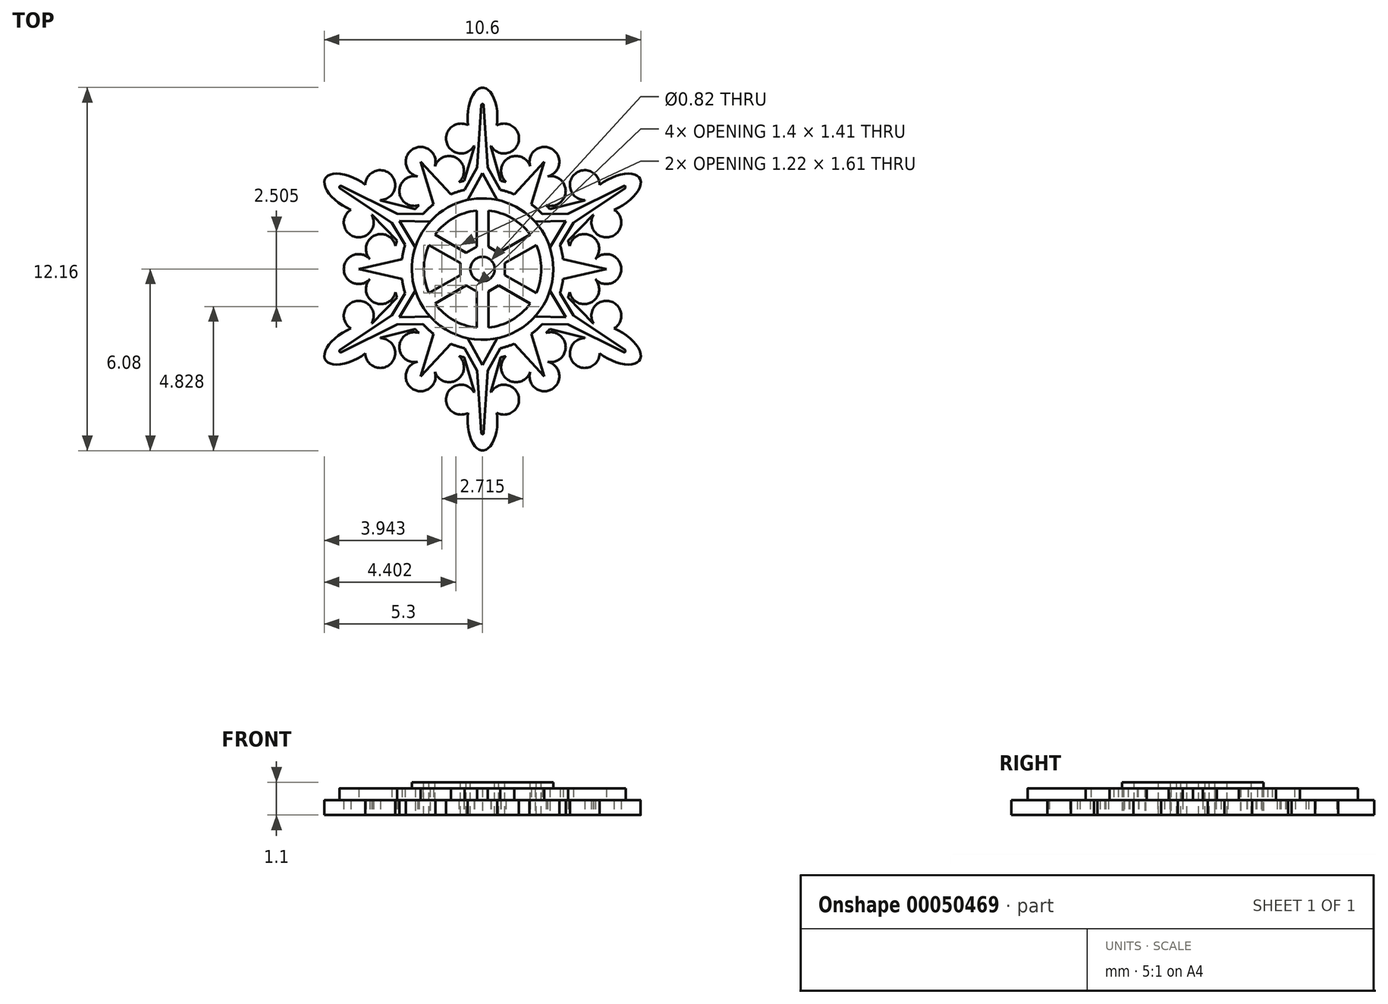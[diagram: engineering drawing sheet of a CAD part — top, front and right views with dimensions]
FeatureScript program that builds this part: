
annotation { "Feature Type Name" : "Feature", "Feature Type Description" : "" }
export const myFeature = defineFeature(function(context is Context, id is Id, definition is map)
    precondition{}
    {
        {
            var Q0;
            Q0=qCreatedBy(makeId("Top.planeOp"),FACE);
            var sketch = newSketch(context, id + "F0", { "sketchPlane" : qUnion([Q0])});
            skArc(sketch, "E0", {"start": v(2.18, 3.1) * mm, "mid": v(2.32, 4.02) * mm, "end": v(1.6, 3.44) * mm});
            skArc(sketch, "E1", {"start": v(2.13, 2.14) * mm, "mid": v(2.78, 2.59) * mm, "end": v(2.18, 3.1) * mm});
            skArc(sketch, "E2", {"start": v(-0.48, 4.81) * mm, "mid": v(-1.2, 4.24) * mm, "end": v(-0.29, 4.12) * mm});
            skLineSegment(sketch, "E3", {"start": v(0, 0) * mm, "end": v(0, 5.06) * mm, "construction": true});
            skLineSegment(sketch, "E4", {"start": v(0, 0) * mm, "end": v(4.69, 2.7) * mm, "construction": true});
            skLineSegment(sketch, "E5", {"start": v(4.69, 2.7) * mm, "end": v(4.69, 0) * mm, "construction": true});
            skLineSegment(sketch, "E6", {"start": v(4.69, 0) * mm, "end": v(0, 0) * mm, "construction": true});
            skArc(sketch, "E7", {"start": v(-0.61, 2.96) * mm, "mid": v(-0.7, 2.94) * mm, "end": v(-0.79, 2.91) * mm});
            skLineSegment(sketch, "E8", {"start": v(0, 0) * mm, "end": v(2.07, 3.6) * mm, "construction": true});
            skLineSegment(sketch, "E9", {"start": v(1.5, 2.61) * mm, "end": v(1.12, 3.29) * mm, "construction": true});
            skLineSegment(sketch, "E10", {"start": v(2.28, 2.61) * mm, "end": v(1.5, 2.61) * mm, "construction": true});
            skLineSegment(sketch, "E11", {"start": v(0, 3.96) * mm, "end": v(-0.72, 4.37) * mm, "construction": true});
            skLineSegment(sketch, "E12", {"start": v(0.72, 4.37) * mm, "end": v(0, 3.96) * mm, "construction": true});
            skArc(sketch, "E13.trimOffspring", {"start": v(0.29, 4.12) * mm, "mid": v(1.2, 4.24) * mm, "end": v(0.48, 4.81) * mm});
            skLineSegment(sketch, "E14.trimOffspring", {"start": v(0.27, 4.11) * mm, "end": v(0.61, 2.96) * mm});
            skLineSegment(sketch, "E15.trimOffspring", {"start": v(-0.27, 4.11) * mm, "end": v(-0.61, 2.96) * mm});
            skLineSegment(sketch, "E16", {"start": v(-0.29, 4.12) * mm, "end": v(-0.27, 4.11) * mm});
            skLineSegment(sketch, "E17", {"start": v(0.29, 4.12) * mm, "end": v(0.27, 4.11) * mm});
            skArc(sketch, "E18.trimOffspring", {"start": v(0.79, 2.91) * mm, "mid": v(0.7, 2.94) * mm, "end": v(0.61, 2.96) * mm});
            skArc(sketch, "E19.trimOffspring", {"start": v(1.6, 3.44) * mm, "mid": v(0.85, 3.7) * mm, "end": v(0.79, 2.91) * mm});
            skEllipticalArc(sketch, "E20", {});
            skArc(sketch, "E21.1.0", {"start": v(-1.6, 3.44) * mm, "mid": v(-2.32, 4.02) * mm, "end": v(-2.18, 3.1) * mm});
            skLineSegment(sketch, "E21.1.1", {"start": v(-3.7, 1.82) * mm, "end": v(-2.86, 0.95) * mm});
            skArc(sketch, "E21.1.2", {"start": v(-2.18, 3.1) * mm, "mid": v(-2.78, 2.59) * mm, "end": v(-2.13, 2.14) * mm});
            skLineSegment(sketch, "E21.1.3", {"start": v(-1.12, 3.29) * mm, "end": v(-1.5, 2.61) * mm, "construction": true});
            skEllipticalArc(sketch, "E21.1.4", {});
            skArc(sketch, "E21.1.5", {"start": v(-0.79, 2.91) * mm, "mid": v(-0.85, 3.7) * mm, "end": v(-1.6, 3.44) * mm});
            skArc(sketch, "E21.1.6", {"start": v(-3.43, 2.31) * mm, "mid": v(-3.07, 3.16) * mm, "end": v(-3.93, 2.82) * mm});
            skArc(sketch, "E21.1.7", {"start": v(-4.4, 1.99) * mm, "mid": v(-4.27, 1.08) * mm, "end": v(-3.71, 1.81) * mm});
            skLineSegment(sketch, "E21.1.8", {"start": v(-3.43, 2.3) * mm, "end": v(-2.25, 2) * mm});
            skLineSegment(sketch, "E21.1.10", {"start": v(-3.7, 1.82) * mm, "end": v(-3.71, 1.81) * mm});
            skLineSegment(sketch, "E21.1.11", {"start": v(-1.5, 2.61) * mm, "end": v(-2.28, 2.61) * mm, "construction": true});
            skLineSegment(sketch, "E21.1.13", {"start": v(-3.43, 2.31) * mm, "end": v(-3.43, 2.3) * mm});
            skArc(sketch, "E21.1.14", {"start": v(-2.13, 2.14) * mm, "mid": v(-2.2, 2.07) * mm, "end": v(-2.25, 2) * mm});
            skArc(sketch, "E21.2.0", {"start": v(-3.78, 0.34) * mm, "mid": v(-4.65, 0) * mm, "end": v(-3.78, -0.34) * mm});
            skLineSegment(sketch, "E21.2.1", {"start": v(-3.43, -2.3) * mm, "end": v(-2.25, -2) * mm});
            skArc(sketch, "E21.2.2", {"start": v(-3.78, -0.34) * mm, "mid": v(-3.63, -1.12) * mm, "end": v(-2.92, -0.77) * mm});
            skLineSegment(sketch, "E21.2.3", {"start": v(-3.4, 0.67) * mm, "end": v(-3.02, 0) * mm, "construction": true});
            skEllipticalArc(sketch, "E21.2.4", {});
            skArc(sketch, "E21.2.5", {"start": v(-2.92, 0.77) * mm, "mid": v(-3.63, 1.12) * mm, "end": v(-3.78, 0.34) * mm});
            skArc(sketch, "E21.2.6", {"start": v(-3.71, -1.81) * mm, "mid": v(-4.27, -1.08) * mm, "end": v(-4.4, -1.99) * mm});
            skArc(sketch, "E21.2.7", {"start": v(-3.93, -2.82) * mm, "mid": v(-3.07, -3.16) * mm, "end": v(-3.43, -2.31) * mm});
            skLineSegment(sketch, "E21.2.8", {"start": v(-3.7, -1.82) * mm, "end": v(-2.86, -0.95) * mm});
            skLineSegment(sketch, "E21.2.10", {"start": v(-3.43, -2.3) * mm, "end": v(-3.43, -2.31) * mm});
            skLineSegment(sketch, "E21.2.11", {"start": v(-3.02, 0) * mm, "end": v(-3.4, -0.67) * mm, "construction": true});
            skLineSegment(sketch, "E21.2.13", {"start": v(-3.71, -1.81) * mm, "end": v(-3.7, -1.82) * mm});
            skArc(sketch, "E21.2.14", {"start": v(-2.92, -0.77) * mm, "mid": v(-2.9, -0.86) * mm, "end": v(-2.86, -0.95) * mm});
            skArc(sketch, "E21.3.0", {"start": v(-2.18, -3.1) * mm, "mid": v(-2.32, -4.02) * mm, "end": v(-1.6, -3.44) * mm});
            skLineSegment(sketch, "E21.3.1", {"start": v(0.27, -4.11) * mm, "end": v(0.61, -2.96) * mm});
            skArc(sketch, "E21.3.2", {"start": v(-1.6, -3.44) * mm, "mid": v(-0.85, -3.7) * mm, "end": v(-0.79, -2.91) * mm});
            skLineSegment(sketch, "E21.3.3", {"start": v(-2.28, -2.61) * mm, "end": v(-1.5, -2.61) * mm, "construction": true});
            skEllipticalArc(sketch, "E21.3.4", {});
            skArc(sketch, "E21.3.5", {"start": v(-2.13, -2.14) * mm, "mid": v(-2.78, -2.59) * mm, "end": v(-2.18, -3.1) * mm});
            skArc(sketch, "E21.3.6", {"start": v(-0.29, -4.12) * mm, "mid": v(-1.2, -4.24) * mm, "end": v(-0.48, -4.81) * mm});
            skArc(sketch, "E21.3.7", {"start": v(0.48, -4.81) * mm, "mid": v(1.2, -4.24) * mm, "end": v(0.29, -4.12) * mm});
            skLineSegment(sketch, "E21.3.8", {"start": v(-0.27, -4.11) * mm, "end": v(-0.61, -2.96) * mm});
            skLineSegment(sketch, "E21.3.10", {"start": v(0.27, -4.11) * mm, "end": v(0.29, -4.12) * mm});
            skLineSegment(sketch, "E21.3.11", {"start": v(-1.5, -2.61) * mm, "end": v(-1.12, -3.29) * mm, "construction": true});
            skLineSegment(sketch, "E21.3.13", {"start": v(-0.29, -4.12) * mm, "end": v(-0.27, -4.11) * mm});
            skArc(sketch, "E21.3.14", {"start": v(-0.79, -2.91) * mm, "mid": v(-0.7, -2.94) * mm, "end": v(-0.61, -2.96) * mm});
            skArc(sketch, "E21.4.0", {"start": v(1.6, -3.44) * mm, "mid": v(2.32, -4.02) * mm, "end": v(2.18, -3.1) * mm});
            skLineSegment(sketch, "E21.4.1", {"start": v(3.7, -1.82) * mm, "end": v(2.86, -0.95) * mm});
            skArc(sketch, "E21.4.2", {"start": v(2.18, -3.1) * mm, "mid": v(2.78, -2.59) * mm, "end": v(2.13, -2.14) * mm});
            skLineSegment(sketch, "E21.4.3", {"start": v(1.12, -3.29) * mm, "end": v(1.5, -2.61) * mm, "construction": true});
            skEllipticalArc(sketch, "E21.4.4", {});
            skArc(sketch, "E21.4.5", {"start": v(0.79, -2.91) * mm, "mid": v(0.85, -3.7) * mm, "end": v(1.6, -3.44) * mm});
            skArc(sketch, "E21.4.6", {"start": v(3.43, -2.31) * mm, "mid": v(3.07, -3.16) * mm, "end": v(3.93, -2.82) * mm});
            skArc(sketch, "E21.4.7", {"start": v(4.4, -1.99) * mm, "mid": v(4.27, -1.08) * mm, "end": v(3.71, -1.81) * mm});
            skLineSegment(sketch, "E21.4.8", {"start": v(3.43, -2.3) * mm, "end": v(2.25, -2) * mm});
            skLineSegment(sketch, "E21.4.10", {"start": v(3.7, -1.82) * mm, "end": v(3.71, -1.81) * mm});
            skLineSegment(sketch, "E21.4.11", {"start": v(1.5, -2.61) * mm, "end": v(2.28, -2.61) * mm, "construction": true});
            skLineSegment(sketch, "E21.4.13", {"start": v(3.43, -2.31) * mm, "end": v(3.43, -2.3) * mm});
            skArc(sketch, "E21.4.14", {"start": v(2.13, -2.14) * mm, "mid": v(2.2, -2.07) * mm, "end": v(2.25, -2) * mm});
            skArc(sketch, "E21.5.0", {"start": v(3.78, -0.34) * mm, "mid": v(4.65, 0) * mm, "end": v(3.78, 0.34) * mm});
            skLineSegment(sketch, "E21.5.1", {"start": v(3.43, 2.3) * mm, "end": v(2.25, 2) * mm});
            skArc(sketch, "E21.5.2", {"start": v(3.78, 0.34) * mm, "mid": v(3.63, 1.12) * mm, "end": v(2.92, 0.77) * mm});
            skLineSegment(sketch, "E21.5.3", {"start": v(3.4, -0.67) * mm, "end": v(3.02, 0) * mm, "construction": true});
            skEllipticalArc(sketch, "E21.5.4", {});
            skArc(sketch, "E21.5.5", {"start": v(2.92, -0.77) * mm, "mid": v(3.63, -1.12) * mm, "end": v(3.78, -0.34) * mm});
            skArc(sketch, "E21.5.6", {"start": v(3.71, 1.81) * mm, "mid": v(4.27, 1.08) * mm, "end": v(4.4, 1.99) * mm});
            skArc(sketch, "E21.5.7", {"start": v(3.93, 2.82) * mm, "mid": v(3.07, 3.16) * mm, "end": v(3.43, 2.31) * mm});
            skLineSegment(sketch, "E21.5.8", {"start": v(3.7, 1.82) * mm, "end": v(2.86, 0.95) * mm});
            skLineSegment(sketch, "E21.5.10", {"start": v(3.43, 2.3) * mm, "end": v(3.43, 2.31) * mm});
            skLineSegment(sketch, "E21.5.11", {"start": v(3.02, 0) * mm, "end": v(3.4, 0.67) * mm, "construction": true});
            skLineSegment(sketch, "E21.5.13", {"start": v(3.71, 1.81) * mm, "end": v(3.7, 1.82) * mm});
            skArc(sketch, "E21.5.14", {"start": v(2.92, 0.77) * mm, "mid": v(2.9, 0.86) * mm, "end": v(2.86, 0.95) * mm});
            skArc(sketch, "E22.trimOffspring", {"start": v(2.25, 2) * mm, "mid": v(2.2, 2.07) * mm, "end": v(2.13, 2.14) * mm});
            skArc(sketch, "E23.trimOffspring", {"start": v(-2.86, 0.95) * mm, "mid": v(-2.9, 0.86) * mm, "end": v(-2.92, 0.77) * mm});
            skArc(sketch, "E24.trimOffspring", {"start": v(2.86, -0.95) * mm, "mid": v(2.9, -0.86) * mm, "end": v(2.92, -0.77) * mm});
            skArc(sketch, "E25.trimOffspring", {"start": v(0.61, -2.96) * mm, "mid": v(0.7, -2.94) * mm, "end": v(0.79, -2.91) * mm});
            skArc(sketch, "E26.trimOffspring", {"start": v(-2.25, -2) * mm, "mid": v(-2.2, -2.07) * mm, "end": v(-2.13, -2.14) * mm});
            skLineSegment(sketch, "E27", {"start": v(3.43, 2.31) * mm, "end": v(3.43, 2.3) * mm});
            const initialGuessF0  = {"E20": [0, 0.005064967554062605, 0, 1, 0.0010143392719328403, 0.0004990733945554542, 4.460182653638514, 1.8230026535410722], "E21.1.4": [-0.0043863905711621475, 0.002532483777031303, -0.8660254037844386, 0.5, 0.0010143392719328403, 0.0004990733945554542, 4.460182653638514, 1.8230026535410722], "E21.2.4": [-0.004386390571162148, -0.002532483777031301, -0.8660254037844388, -0.5, 0.0010143392719328403, 0.0004990733945554542, 4.460182653638514, 1.823002653541072], "E21.3.4": [0, -0.005064967554062605, 0, -1, 0.0010143392719328403, 0.0004990733945554542, 4.460182653638514, 1.8230026535410724], "E21.4.4": [0.004386390571162147, -0.0025324837770313046, 0.8660254037844384, -0.5, 0.0010143392719328403, 0.0004990733945554542, 4.460182653638514, 1.8230026535410724], "E21.5.4": [0.0043863905711621475, 0.002532483777031303, 0.8660254037844386, 0.5, 0.0010143392719328403, 0.0004990733945554542, 4.460182653638514, 1.8230026535410717]};
            skSetInitialGuess(sketch, initialGuessF0);
            skSolve(sketch);
        }
        {
            var Q0;
            Q0 = qSketchRegion(id + "F0", true);
            extrude(context, id + "F1", {"entities" : qUnion([Q0]), "depth" : .5 * mm});
        }
        {
            var Q0;
            Q0=makeQuery(id+"F1.opExtrude","CAP_FACE",FACE,{"disambiguationData":[OSD([sQuery(id+"F0.wireOp",EDGE,"E0"),sQuery(id+"F0.wireOp",EDGE,"E1"),sQuery(id+"F0.wireOp",EDGE,"E2"),sQuery(id+"F0.wireOp",EDGE,"E7"),sQuery(id+"F0.wireOp",EDGE,"E13.trimOffspring"),sQuery(id+"F0.wireOp",EDGE,"E14.trimOffspring"),sQuery(id+"F0.wireOp",EDGE,"E15.trimOffspring"),sQuery(id+"F0.wireOp",EDGE,"E16"),sQuery(id+"F0.wireOp",EDGE,"E17"),sQuery(id+"F0.wireOp",EDGE,"E18.trimOffspring"),sQuery(id+"F0.wireOp",EDGE,"E19.trimOffspring"),sQuery(id+"F0.wireOp",EDGE,"E20"),sQuery(id+"F0.wireOp",EDGE,"E21.1.0"),sQuery(id+"F0.wireOp",EDGE,"E21.1.1"),sQuery(id+"F0.wireOp",EDGE,"E21.1.2"),sQuery(id+"F0.wireOp",EDGE,"E21.1.4"),sQuery(id+"F0.wireOp",EDGE,"E21.1.5"),sQuery(id+"F0.wireOp",EDGE,"E21.1.6"),sQuery(id+"F0.wireOp",EDGE,"E21.1.7"),sQuery(id+"F0.wireOp",EDGE,"E21.1.8"),sQuery(id+"F0.wireOp",EDGE,"E21.1.10"),sQuery(id+"F0.wireOp",EDGE,"E21.1.13"),sQuery(id+"F0.wireOp",EDGE,"E21.2.0"),sQuery(id+"F0.wireOp",EDGE,"E21.2.1"),sQuery(id+"F0.wireOp",EDGE,"E21.2.2"),sQuery(id+"F0.wireOp",EDGE,"E21.2.4"),sQuery(id+"F0.wireOp",EDGE,"E21.2.5"),sQuery(id+"F0.wireOp",EDGE,"E21.2.6"),sQuery(id+"F0.wireOp",EDGE,"E21.2.7"),sQuery(id+"F0.wireOp",EDGE,"E21.2.8"),sQuery(id+"F0.wireOp",EDGE,"E21.2.10"),sQuery(id+"F0.wireOp",EDGE,"E21.2.13"),sQuery(id+"F0.wireOp",EDGE,"E21.3.0"),sQuery(id+"F0.wireOp",EDGE,"E21.3.1"),sQuery(id+"F0.wireOp",EDGE,"E21.3.2"),sQuery(id+"F0.wireOp",EDGE,"E21.3.4"),sQuery(id+"F0.wireOp",EDGE,"E21.3.5"),sQuery(id+"F0.wireOp",EDGE,"E21.3.6"),sQuery(id+"F0.wireOp",EDGE,"E21.3.7"),sQuery(id+"F0.wireOp",EDGE,"E21.3.8"),sQuery(id+"F0.wireOp",EDGE,"E21.3.10"),sQuery(id+"F0.wireOp",EDGE,"E21.3.13"),sQuery(id+"F0.wireOp",EDGE,"E21.4.0"),sQuery(id+"F0.wireOp",EDGE,"E21.4.1"),sQuery(id+"F0.wireOp",EDGE,"E21.4.2"),sQuery(id+"F0.wireOp",EDGE,"E21.4.4"),sQuery(id+"F0.wireOp",EDGE,"E21.4.5"),sQuery(id+"F0.wireOp",EDGE,"E21.4.6"),sQuery(id+"F0.wireOp",EDGE,"E21.4.7"),sQuery(id+"F0.wireOp",EDGE,"E21.4.8"),sQuery(id+"F0.wireOp",EDGE,"E21.4.10"),sQuery(id+"F0.wireOp",EDGE,"E21.4.13"),sQuery(id+"F0.wireOp",EDGE,"E21.5.0"),sQuery(id+"F0.wireOp",EDGE,"E21.5.1"),sQuery(id+"F0.wireOp",EDGE,"E21.5.2"),sQuery(id+"F0.wireOp",EDGE,"E21.5.4"),sQuery(id+"F0.wireOp",EDGE,"E21.5.5"),sQuery(id+"F0.wireOp",EDGE,"E21.5.6"),sQuery(id+"F0.wireOp",EDGE,"E21.5.7"),sQuery(id+"F0.wireOp",EDGE,"E21.5.8"),sQuery(id+"F0.wireOp",EDGE,"E21.5.13"),sQuery(id+"F0.wireOp",EDGE,"E22.trimOffspring"),sQuery(id+"F0.wireOp",EDGE,"E23.trimOffspring"),sQuery(id+"F0.wireOp",EDGE,"E24.trimOffspring"),sQuery(id+"F0.wireOp",EDGE,"E25.trimOffspring"),sQuery(id+"F0.wireOp",EDGE,"E26.trimOffspring"),sQuery(id+"F0.wireOp",EDGE,"E21.5.14"),sQuery(id+"F0.wireOp",EDGE,"E21.4.14"),sQuery(id+"F0.wireOp",EDGE,"E21.3.14"),sQuery(id+"F0.wireOp",EDGE,"E21.2.14"),sQuery(id+"F0.wireOp",EDGE,"E21.1.14"),sQuery(id+"F0.wireOp",EDGE,"E27")])],"isStart":false});
            var sketch = newSketch(context, id + "F2", { "sketchPlane" : qUnion([Q0])});
            skArc(sketch, "E28", {"start": v(-0.6, 2.65) * mm, "mid": v(-1.36, 2.35) * mm, "end": v(-2, 1.84) * mm});
            skLineSegment(sketch, "E29", {"start": v(-0.6, 2.65) * mm, "end": v(-0.18, 3.4) * mm});
            skLineSegment(sketch, "E30", {"start": v(0.18, 3.4) * mm, "end": v(0.6, 2.65) * mm});
            skLineSegment(sketch, "E31", {"start": v(-0.18, 3.4) * mm, "end": v(-0.04, 5.49) * mm});
            skLineSegment(sketch, "E32", {"start": v(0.04, 5.49) * mm, "end": v(0.18, 3.4) * mm});
            skPoint(sketch, "E33.visualSharp", {"position": v(0, 6.08) * mm});
            skArc(sketch, "E33.filletArc", {"start": v(0.04, 5.49) * mm, "mid": v(0, 5.53) * mm, "end": v(-0.04, 5.49) * mm});
            skPoint(sketch, "E34.orphan", {"position": v(0, 3.74) * mm});
            skLineSegment(sketch, "E35.1.0", {"start": v(-2.6, 0.8) * mm, "end": v(-3.04, 1.55) * mm});
            skLineSegment(sketch, "E35.1.1", {"start": v(-3.04, 1.55) * mm, "end": v(-4.77, 2.71) * mm});
            skLineSegment(sketch, "E35.1.2", {"start": v(-4.73, 2.78) * mm, "end": v(-2.86, 1.86) * mm});
            skLineSegment(sketch, "E35.1.3", {"start": v(-2.86, 1.86) * mm, "end": v(-2, 1.84) * mm});
            skArc(sketch, "E35.1.4", {"start": v(-4.73, 2.78) * mm, "mid": v(-4.79, 2.76) * mm, "end": v(-4.77, 2.71) * mm});
            skLineSegment(sketch, "E35.2.0", {"start": v(-2, -1.84) * mm, "end": v(-2.86, -1.86) * mm});
            skLineSegment(sketch, "E35.2.1", {"start": v(-2.86, -1.86) * mm, "end": v(-4.73, -2.78) * mm});
            skLineSegment(sketch, "E35.2.2", {"start": v(-4.77, -2.71) * mm, "end": v(-3.04, -1.55) * mm});
            skLineSegment(sketch, "E35.2.3", {"start": v(-3.04, -1.55) * mm, "end": v(-2.6, -0.8) * mm});
            skArc(sketch, "E35.2.4", {"start": v(-4.77, -2.71) * mm, "mid": v(-4.79, -2.76) * mm, "end": v(-4.73, -2.78) * mm});
            skLineSegment(sketch, "E35.3.0", {"start": v(0.6, -2.65) * mm, "end": v(0.18, -3.4) * mm});
            skLineSegment(sketch, "E35.3.1", {"start": v(0.18, -3.4) * mm, "end": v(0.04, -5.49) * mm});
            skLineSegment(sketch, "E35.3.2", {"start": v(-0.04, -5.49) * mm, "end": v(-0.18, -3.4) * mm});
            skLineSegment(sketch, "E35.3.3", {"start": v(-0.18, -3.4) * mm, "end": v(-0.6, -2.65) * mm});
            skArc(sketch, "E35.3.4", {"start": v(-0.04, -5.49) * mm, "mid": v(0, -5.53) * mm, "end": v(0.04, -5.49) * mm});
            skLineSegment(sketch, "E35.4.0", {"start": v(2.6, -0.8) * mm, "end": v(3.04, -1.55) * mm});
            skLineSegment(sketch, "E35.4.1", {"start": v(3.04, -1.55) * mm, "end": v(4.77, -2.71) * mm});
            skLineSegment(sketch, "E35.4.2", {"start": v(4.73, -2.78) * mm, "end": v(2.86, -1.86) * mm});
            skLineSegment(sketch, "E35.4.3", {"start": v(2.86, -1.86) * mm, "end": v(2, -1.84) * mm});
            skArc(sketch, "E35.4.4", {"start": v(4.73, -2.78) * mm, "mid": v(4.79, -2.76) * mm, "end": v(4.77, -2.71) * mm});
            skLineSegment(sketch, "E35.5.0", {"start": v(2, 1.84) * mm, "end": v(2.86, 1.86) * mm});
            skLineSegment(sketch, "E35.5.1", {"start": v(2.86, 1.86) * mm, "end": v(4.73, 2.78) * mm});
            skLineSegment(sketch, "E35.5.2", {"start": v(4.77, 2.71) * mm, "end": v(3.04, 1.55) * mm});
            skLineSegment(sketch, "E35.5.3", {"start": v(3.04, 1.55) * mm, "end": v(2.6, 0.8) * mm});
            skArc(sketch, "E35.5.4", {"start": v(4.77, 2.71) * mm, "mid": v(4.79, 2.76) * mm, "end": v(4.73, 2.78) * mm});
            skArc(sketch, "E36.trimOffspring", {"start": v(2, 1.84) * mm, "mid": v(1.36, 2.35) * mm, "end": v(0.6, 2.65) * mm});
            skArc(sketch, "E37.trimOffspring", {"start": v(-2.6, 0.8) * mm, "mid": v(-2.72, 0) * mm, "end": v(-2.6, -0.8) * mm});
            skArc(sketch, "E38.trimOffspring", {"start": v(2.6, -0.8) * mm, "mid": v(2.72, 0) * mm, "end": v(2.6, 0.8) * mm});
            skArc(sketch, "E39.trimOffspring", {"start": v(0.6, -2.65) * mm, "mid": v(1.36, -2.35) * mm, "end": v(2, -1.84) * mm});
            skArc(sketch, "E40.trimOffspring", {"start": v(-2, -1.84) * mm, "mid": v(-1.36, -2.35) * mm, "end": v(-0.6, -2.65) * mm});
            skLineSegment(sketch, "E41", {"start": v(0, 3.22) * mm, "end": v(0.55, 2.22) * mm});
            skLineSegment(sketch, "E42", {"start": v(0.55, 2.22) * mm, "end": v(-0.55, 2.22) * mm});
            skLineSegment(sketch, "E43", {"start": v(-0.55, 2.22) * mm, "end": v(0, 3.22) * mm});
            skLineSegment(sketch, "E44.1.0", {"start": v(-2.2, 0.63) * mm, "end": v(-2.79, 1.6) * mm});
            skLineSegment(sketch, "E44.1.1", {"start": v(-2.79, 1.6) * mm, "end": v(-1.65, 1.59) * mm});
            skLineSegment(sketch, "E44.1.2", {"start": v(-1.65, 1.59) * mm, "end": v(-2.2, 0.63) * mm});
            skLineSegment(sketch, "E44.2.0", {"start": v(-1.65, -1.59) * mm, "end": v(-2.79, -1.6) * mm});
            skLineSegment(sketch, "E44.2.1", {"start": v(-2.79, -1.6) * mm, "end": v(-2.2, -0.63) * mm});
            skLineSegment(sketch, "E44.2.2", {"start": v(-2.2, -0.63) * mm, "end": v(-1.65, -1.59) * mm});
            skLineSegment(sketch, "E44.3.0", {"start": v(0.55, -2.22) * mm, "end": v(0, -3.22) * mm});
            skLineSegment(sketch, "E44.3.1", {"start": v(0, -3.22) * mm, "end": v(-0.55, -2.22) * mm});
            skLineSegment(sketch, "E44.3.2", {"start": v(-0.55, -2.22) * mm, "end": v(0.55, -2.22) * mm});
            skLineSegment(sketch, "E44.4.0", {"start": v(2.2, -0.63) * mm, "end": v(2.79, -1.6) * mm});
            skLineSegment(sketch, "E44.4.1", {"start": v(2.79, -1.6) * mm, "end": v(1.65, -1.59) * mm});
            skLineSegment(sketch, "E44.4.2", {"start": v(1.65, -1.59) * mm, "end": v(2.2, -0.63) * mm});
            skLineSegment(sketch, "E44.5.0", {"start": v(1.65, 1.59) * mm, "end": v(2.79, 1.6) * mm});
            skLineSegment(sketch, "E44.5.1", {"start": v(2.79, 1.6) * mm, "end": v(2.2, 0.63) * mm});
            skLineSegment(sketch, "E44.5.2", {"start": v(2.2, 0.63) * mm, "end": v(1.65, 1.59) * mm});
            skLineSegment(sketch, "E45", {"start": v(2.07, 3.6) * mm, "end": v(1.64, 2.17) * mm});
            skLineSegment(sketch, "E46", {"start": v(2.07, 3.6) * mm, "end": v(1.06, 2.5) * mm});
            skLineSegment(sketch, "E47.1.0", {"start": v(-2.07, 3.6) * mm, "end": v(-1.64, 2.17) * mm});
            skLineSegment(sketch, "E47.1.1", {"start": v(-2.07, 3.6) * mm, "end": v(-1.06, 2.5) * mm});
            skLineSegment(sketch, "E47.2.0", {"start": v(-4.15, 0) * mm, "end": v(-2.7, -0.34) * mm});
            skLineSegment(sketch, "E47.2.1", {"start": v(-4.15, 0) * mm, "end": v(-2.7, 0.34) * mm});
            skLineSegment(sketch, "E47.3.0", {"start": v(-2.07, -3.6) * mm, "end": v(-1.06, -2.5) * mm});
            skLineSegment(sketch, "E47.3.1", {"start": v(-2.07, -3.6) * mm, "end": v(-1.64, -2.17) * mm});
            skLineSegment(sketch, "E47.4.0", {"start": v(2.07, -3.6) * mm, "end": v(1.64, -2.17) * mm});
            skLineSegment(sketch, "E47.4.1", {"start": v(2.07, -3.6) * mm, "end": v(1.06, -2.5) * mm});
            skLineSegment(sketch, "E47.5.0", {"start": v(4.15, 0) * mm, "end": v(2.7, 0.34) * mm});
            skLineSegment(sketch, "E47.5.1", {"start": v(4.15, 0) * mm, "end": v(2.7, -0.34) * mm});
            skSolve(sketch);
        }
        {
            var Q0;
            Q0 = qSketchRegion(id + "F2", true);
            extrude(context, id + "F3", {"entities" : qUnion([Q0]), "operationType" : NewBodyOperationType.ADD, "depth" : .4 * mm});
        }
        {
            var Q0;
            Q0=makeQuery(id+"F3.opExtrude","CAP_FACE",FACE,{"disambiguationData":[OSD([sQuery(id+"F2.wireOp",EDGE,"E28"),sQuery(id+"F2.wireOp",EDGE,"E29"),sQuery(id+"F2.wireOp",EDGE,"E30"),sQuery(id+"F2.wireOp",EDGE,"E31"),sQuery(id+"F2.wireOp",EDGE,"E32"),sQuery(id+"F2.wireOp",EDGE,"E33.filletArc"),sQuery(id+"F2.wireOp",EDGE,"E35.1.0"),sQuery(id+"F2.wireOp",EDGE,"E35.1.1"),sQuery(id+"F2.wireOp",EDGE,"E35.1.2"),sQuery(id+"F2.wireOp",EDGE,"E35.1.3"),sQuery(id+"F2.wireOp",EDGE,"E35.1.4"),sQuery(id+"F2.wireOp",EDGE,"E35.2.0"),sQuery(id+"F2.wireOp",EDGE,"E35.2.1"),sQuery(id+"F2.wireOp",EDGE,"E35.2.2"),sQuery(id+"F2.wireOp",EDGE,"E35.2.3"),sQuery(id+"F2.wireOp",EDGE,"E35.2.4"),sQuery(id+"F2.wireOp",EDGE,"E35.3.0"),sQuery(id+"F2.wireOp",EDGE,"E35.3.1"),sQuery(id+"F2.wireOp",EDGE,"E35.3.2"),sQuery(id+"F2.wireOp",EDGE,"E35.3.3"),sQuery(id+"F2.wireOp",EDGE,"E35.3.4"),sQuery(id+"F2.wireOp",EDGE,"E35.4.0"),sQuery(id+"F2.wireOp",EDGE,"E35.4.1"),sQuery(id+"F2.wireOp",EDGE,"E35.4.2"),sQuery(id+"F2.wireOp",EDGE,"E35.4.3"),sQuery(id+"F2.wireOp",EDGE,"E35.4.4"),sQuery(id+"F2.wireOp",EDGE,"E35.5.0"),sQuery(id+"F2.wireOp",EDGE,"E35.5.1"),sQuery(id+"F2.wireOp",EDGE,"E35.5.2"),sQuery(id+"F2.wireOp",EDGE,"E35.5.3"),sQuery(id+"F2.wireOp",EDGE,"E35.5.4"),sQuery(id+"F2.wireOp",EDGE,"E36.trimOffspring"),sQuery(id+"F2.wireOp",EDGE,"E37.trimOffspring"),sQuery(id+"F2.wireOp",EDGE,"E38.trimOffspring"),sQuery(id+"F2.wireOp",EDGE,"E39.trimOffspring"),sQuery(id+"F2.wireOp",EDGE,"E40.trimOffspring"),sQuery(id+"F2.wireOp",EDGE,"E41"),sQuery(id+"F2.wireOp",EDGE,"E42"),sQuery(id+"F2.wireOp",EDGE,"E43"),sQuery(id+"F2.wireOp",EDGE,"E44.1.0"),sQuery(id+"F2.wireOp",EDGE,"E44.1.1"),sQuery(id+"F2.wireOp",EDGE,"E44.1.2"),sQuery(id+"F2.wireOp",EDGE,"E44.2.0"),sQuery(id+"F2.wireOp",EDGE,"E44.2.1"),sQuery(id+"F2.wireOp",EDGE,"E44.2.2"),sQuery(id+"F2.wireOp",EDGE,"E44.3.0"),sQuery(id+"F2.wireOp",EDGE,"E44.3.1"),sQuery(id+"F2.wireOp",EDGE,"E44.3.2"),sQuery(id+"F2.wireOp",EDGE,"E44.4.0"),sQuery(id+"F2.wireOp",EDGE,"E44.4.1"),sQuery(id+"F2.wireOp",EDGE,"E44.4.2"),sQuery(id+"F2.wireOp",EDGE,"E44.5.0"),sQuery(id+"F2.wireOp",EDGE,"E44.5.1"),sQuery(id+"F2.wireOp",EDGE,"E44.5.2")])],"isStart":false});
            var sketch = newSketch(context, id + "F4", { "sketchPlane" : qUnion([Q0])});
            skCircle(sketch, "E48", {"center": v(0, 0) * mm, "radius": 2.37 * mm});
            skSolve(sketch);
        }
        {
            var Q0;
            Q0 = qSketchRegion(id + "F4", true);
            extrude(context, id + "F5", {"entities" : qUnion([Q0]), "operationType" : NewBodyOperationType.ADD, "depth" : .2 * mm, "hasSecondDirection" : true, "secondDirectionBound" : BoundingType.UP_TO_NEXT, "secondDirectionOppositeDirection" : true, "secondDirectionDepth" : 25 * mm});
        }
        {
            var Q0;
            Q0=makeQuery(id+"F5.opExtrude","CAP_FACE",FACE,{"disambiguationData":[OSD([sQuery(id+"F4.wireOp",EDGE,"E48")])],"isStart":false});
            var sketch = newSketch(context, id + "F6", { "sketchPlane" : qUnion([Q0])});
            skArc(sketch, "E49", {"start": v(-0.2, 1.96) * mm, "mid": v(-0.98, 1.7) * mm, "end": v(-1.6, 1.15) * mm});
            skLineSegment(sketch, "E50", {"start": v(-0.2, 1.96) * mm, "end": v(-0.2, 0.75) * mm});
            skLineSegment(sketch, "E51.1.0", {"start": v(-1.8, 0.8) * mm, "end": v(-0.75, 0.2) * mm});
            skLineSegment(sketch, "E51.2.0", {"start": v(-1.6, -1.15) * mm, "end": v(-0.55, -0.55) * mm});
            skLineSegment(sketch, "E51.3.0", {"start": v(0.2, -1.96) * mm, "end": v(0.2, -0.75) * mm});
            skLineSegment(sketch, "E51.4.0", {"start": v(1.8, -0.8) * mm, "end": v(0.75, -0.2) * mm});
            skLineSegment(sketch, "E51.5.0", {"start": v(1.6, 1.15) * mm, "end": v(0.55, 0.55) * mm});
            skArc(sketch, "E52.trimOffspring", {"start": v(-1.8, 0.8) * mm, "mid": v(-1.97, 0) * mm, "end": v(-1.8, -0.8) * mm});
            skArc(sketch, "E53.trimOffspring", {"start": v(-1.6, -1.15) * mm, "mid": v(-0.98, -1.7) * mm, "end": v(-0.2, -1.96) * mm});
            skArc(sketch, "E54.trimOffspring", {"start": v(0.2, -1.96) * mm, "mid": v(0.98, -1.7) * mm, "end": v(1.6, -1.15) * mm});
            skArc(sketch, "E55.trimOffspring", {"start": v(1.8, -0.8) * mm, "mid": v(1.97, 0) * mm, "end": v(1.8, 0.8) * mm});
            skArc(sketch, "E56.trimOffspring", {"start": v(1.6, 1.15) * mm, "mid": v(0.98, 1.7) * mm, "end": v(0.2, 1.96) * mm});
            skLineSegment(sketch, "E57.trimOffspring", {"start": v(0.2, 0.75) * mm, "end": v(0.2, 1.96) * mm});
            skLineSegment(sketch, "E58.trimOffspring", {"start": v(-0.55, 0.55) * mm, "end": v(-1.6, 1.15) * mm});
            skLineSegment(sketch, "E59.trimOffspring", {"start": v(-0.75, -0.2) * mm, "end": v(-1.8, -0.8) * mm});
            skLineSegment(sketch, "E60.trimOffspring", {"start": v(-0.2, -0.75) * mm, "end": v(-0.2, -1.96) * mm});
            skLineSegment(sketch, "E61.trimOffspring", {"start": v(0.55, -0.55) * mm, "end": v(1.6, -1.15) * mm});
            skLineSegment(sketch, "E62.trimOffspring", {"start": v(0.75, 0.2) * mm, "end": v(1.8, 0.8) * mm});
            skLineSegment(sketch, "E63", {"start": v(-0.55, 0.55) * mm, "end": v(-0.2, 0.75) * mm});
            skPoint(sketch, "E64.trimOffspring.end.orphan", {"position": v(-0.2, 0) * mm});
            skLineSegment(sketch, "E65.1.0", {"start": v(-0.75, -0.2) * mm, "end": v(-0.75, 0.2) * mm});
            skLineSegment(sketch, "E65.2.0", {"start": v(-0.2, -0.75) * mm, "end": v(-0.55, -0.55) * mm});
            skLineSegment(sketch, "E65.3.0", {"start": v(0.55, -0.55) * mm, "end": v(0.2, -0.75) * mm});
            skLineSegment(sketch, "E65.4.0", {"start": v(0.75, 0.2) * mm, "end": v(0.75, -0.2) * mm});
            skLineSegment(sketch, "E65.5.0", {"start": v(0.2, 0.75) * mm, "end": v(0.55, 0.55) * mm});
            skPoint(sketch, "E66.orphan", {"position": v(-0.2, 0.35) * mm});
            skCircle(sketch, "E67", {"center": v(0, 0) * mm, "radius": 0.4 * mm});
            skSolve(sketch);
        }
        {
            var Q0;
            Q0 = qSketchRegion(id + "F6", true);
            extrude(context, id + "F7", {"entities" : qUnion([Q0]), "operationType" : NewBodyOperationType.REMOVE, "endBound" : BoundingType.UP_TO_NEXT, "oppositeDirection" : true, "depth" : 25 * mm});
        }
        {
            var Q0;
            Q0=makeQuery(id+"F3.boolean.opBoolean","SPLIT",FACE,{"disambiguationData":[TD([makeQuery(id+"F3.opExtrude","SWEPT_FACE",FACE,{"disambiguationData":[OSD([sQuery(id+"F2.wireOp",EDGE,"E41")])]})])],"derivedFrom":makeQuery(id+"F1.opExtrude","CAP_FACE",FACE,{"disambiguationData":[OSD([sQuery(id+"F0.wireOp",EDGE,"E0"),sQuery(id+"F0.wireOp",EDGE,"E1"),sQuery(id+"F0.wireOp",EDGE,"E2"),sQuery(id+"F0.wireOp",EDGE,"E7"),sQuery(id+"F0.wireOp",EDGE,"E13.trimOffspring"),sQuery(id+"F0.wireOp",EDGE,"E14.trimOffspring"),sQuery(id+"F0.wireOp",EDGE,"E15.trimOffspring"),sQuery(id+"F0.wireOp",EDGE,"E16"),sQuery(id+"F0.wireOp",EDGE,"E17"),sQuery(id+"F0.wireOp",EDGE,"E18.trimOffspring"),sQuery(id+"F0.wireOp",EDGE,"E19.trimOffspring"),sQuery(id+"F0.wireOp",EDGE,"E20"),sQuery(id+"F0.wireOp",EDGE,"E21.1.0"),sQuery(id+"F0.wireOp",EDGE,"E21.1.1"),sQuery(id+"F0.wireOp",EDGE,"E21.1.2"),sQuery(id+"F0.wireOp",EDGE,"E21.1.4"),sQuery(id+"F0.wireOp",EDGE,"E21.1.5"),sQuery(id+"F0.wireOp",EDGE,"E21.1.6"),sQuery(id+"F0.wireOp",EDGE,"E21.1.7"),sQuery(id+"F0.wireOp",EDGE,"E21.1.8"),sQuery(id+"F0.wireOp",EDGE,"E21.1.10"),sQuery(id+"F0.wireOp",EDGE,"E21.1.13"),sQuery(id+"F0.wireOp",EDGE,"E21.2.0"),sQuery(id+"F0.wireOp",EDGE,"E21.2.1"),sQuery(id+"F0.wireOp",EDGE,"E21.2.2"),sQuery(id+"F0.wireOp",EDGE,"E21.2.4"),sQuery(id+"F0.wireOp",EDGE,"E21.2.5"),sQuery(id+"F0.wireOp",EDGE,"E21.2.6"),sQuery(id+"F0.wireOp",EDGE,"E21.2.7"),sQuery(id+"F0.wireOp",EDGE,"E21.2.8"),sQuery(id+"F0.wireOp",EDGE,"E21.2.10"),sQuery(id+"F0.wireOp",EDGE,"E21.2.13"),sQuery(id+"F0.wireOp",EDGE,"E21.3.0"),sQuery(id+"F0.wireOp",EDGE,"E21.3.1"),sQuery(id+"F0.wireOp",EDGE,"E21.3.2"),sQuery(id+"F0.wireOp",EDGE,"E21.3.4"),sQuery(id+"F0.wireOp",EDGE,"E21.3.5"),sQuery(id+"F0.wireOp",EDGE,"E21.3.6"),sQuery(id+"F0.wireOp",EDGE,"E21.3.7"),sQuery(id+"F0.wireOp",EDGE,"E21.3.8"),sQuery(id+"F0.wireOp",EDGE,"E21.3.10"),sQuery(id+"F0.wireOp",EDGE,"E21.3.13"),sQuery(id+"F0.wireOp",EDGE,"E21.4.0"),sQuery(id+"F0.wireOp",EDGE,"E21.4.1"),sQuery(id+"F0.wireOp",EDGE,"E21.4.2"),sQuery(id+"F0.wireOp",EDGE,"E21.4.4"),sQuery(id+"F0.wireOp",EDGE,"E21.4.5"),sQuery(id+"F0.wireOp",EDGE,"E21.4.6"),sQuery(id+"F0.wireOp",EDGE,"E21.4.7"),sQuery(id+"F0.wireOp",EDGE,"E21.4.8"),sQuery(id+"F0.wireOp",EDGE,"E21.4.10"),sQuery(id+"F0.wireOp",EDGE,"E21.4.13"),sQuery(id+"F0.wireOp",EDGE,"E21.5.0"),sQuery(id+"F0.wireOp",EDGE,"E21.5.1"),sQuery(id+"F0.wireOp",EDGE,"E21.5.2"),sQuery(id+"F0.wireOp",EDGE,"E21.5.4"),sQuery(id+"F0.wireOp",EDGE,"E21.5.5"),sQuery(id+"F0.wireOp",EDGE,"E21.5.6"),sQuery(id+"F0.wireOp",EDGE,"E21.5.7"),sQuery(id+"F0.wireOp",EDGE,"E21.5.8"),sQuery(id+"F0.wireOp",EDGE,"E21.5.13"),sQuery(id+"F0.wireOp",EDGE,"E22.trimOffspring"),sQuery(id+"F0.wireOp",EDGE,"E23.trimOffspring"),sQuery(id+"F0.wireOp",EDGE,"E24.trimOffspring"),sQuery(id+"F0.wireOp",EDGE,"E25.trimOffspring"),sQuery(id+"F0.wireOp",EDGE,"E26.trimOffspring"),sQuery(id+"F0.wireOp",EDGE,"E21.5.14"),sQuery(id+"F0.wireOp",EDGE,"E21.4.14"),sQuery(id+"F0.wireOp",EDGE,"E21.3.14"),sQuery(id+"F0.wireOp",EDGE,"E21.2.14"),sQuery(id+"F0.wireOp",EDGE,"E21.1.14"),sQuery(id+"F0.wireOp",EDGE,"E27")])],"isStart":false})});
            var sketch = newSketch(context, id + "F8", { "sketchPlane" : qUnion([Q0])});
            skLineSegment(sketch, "E68.0", {"start": v(0, 3.22) * mm, "end": v(0.5, 2.32) * mm});
            skLineSegment(sketch, "E68.1", {"start": v(-0.5, 2.32) * mm, "end": v(0, 3.22) * mm});
            skArc(sketch, "E68.2", {"start": v(-1.76, 1.59) * mm, "mid": v(-2.05, 1.18) * mm, "end": v(-2.25, 0.73) * mm});
            skLineSegment(sketch, "E69.0", {"start": v(1.76, 1.59) * mm, "end": v(2.79, 1.6) * mm});
            skLineSegment(sketch, "E69.1", {"start": v(2.79, 1.6) * mm, "end": v(2.25, 0.73) * mm});
            skLineSegment(sketch, "E70.0", {"start": v(2.25, -0.73) * mm, "end": v(2.79, -1.6) * mm});
            skLineSegment(sketch, "E70.1", {"start": v(2.79, -1.6) * mm, "end": v(1.76, -1.59) * mm});
            skLineSegment(sketch, "E70.2", {"start": v(0.5, -2.32) * mm, "end": v(0, -3.22) * mm});
            skLineSegment(sketch, "E70.3", {"start": v(0, -3.22) * mm, "end": v(-0.5, -2.32) * mm});
            skLineSegment(sketch, "E70.4", {"start": v(-1.76, -1.59) * mm, "end": v(-2.79, -1.6) * mm});
            skLineSegment(sketch, "E70.5", {"start": v(-2.79, -1.6) * mm, "end": v(-2.25, -0.73) * mm});
            skLineSegment(sketch, "E70.6", {"start": v(-2.25, 0.73) * mm, "end": v(-2.79, 1.6) * mm});
            skLineSegment(sketch, "E70.7", {"start": v(-2.79, 1.6) * mm, "end": v(-1.76, 1.59) * mm});
            skArc(sketch, "E71.trimOffspring", {"start": v(0.5, 2.32) * mm, "mid": v(0, 2.37) * mm, "end": v(-0.5, 2.32) * mm});
            skArc(sketch, "E72.trimOffspring", {"start": v(2.25, 0.73) * mm, "mid": v(2.05, 1.18) * mm, "end": v(1.76, 1.59) * mm});
            skArc(sketch, "E73.trimOffspring", {"start": v(1.76, -1.59) * mm, "mid": v(2.05, -1.18) * mm, "end": v(2.25, -0.73) * mm});
            skArc(sketch, "E74.trimOffspring", {"start": v(-0.5, -2.32) * mm, "mid": v(0, -2.37) * mm, "end": v(0.5, -2.32) * mm});
            skArc(sketch, "E75.trimOffspring", {"start": v(-2.25, -0.73) * mm, "mid": v(-2.05, -1.18) * mm, "end": v(-1.76, -1.59) * mm});
            skSolve(sketch);
        }
        {
            var Q0;
            Q0 = qSketchRegion(id + "F8", true);
            extrude(context, id + "F9", {"entities" : qUnion([Q0]), "operationType" : NewBodyOperationType.REMOVE, "endBound" : BoundingType.UP_TO_NEXT, "oppositeDirection" : true, "depth" : 25 * mm});
        }
    });
